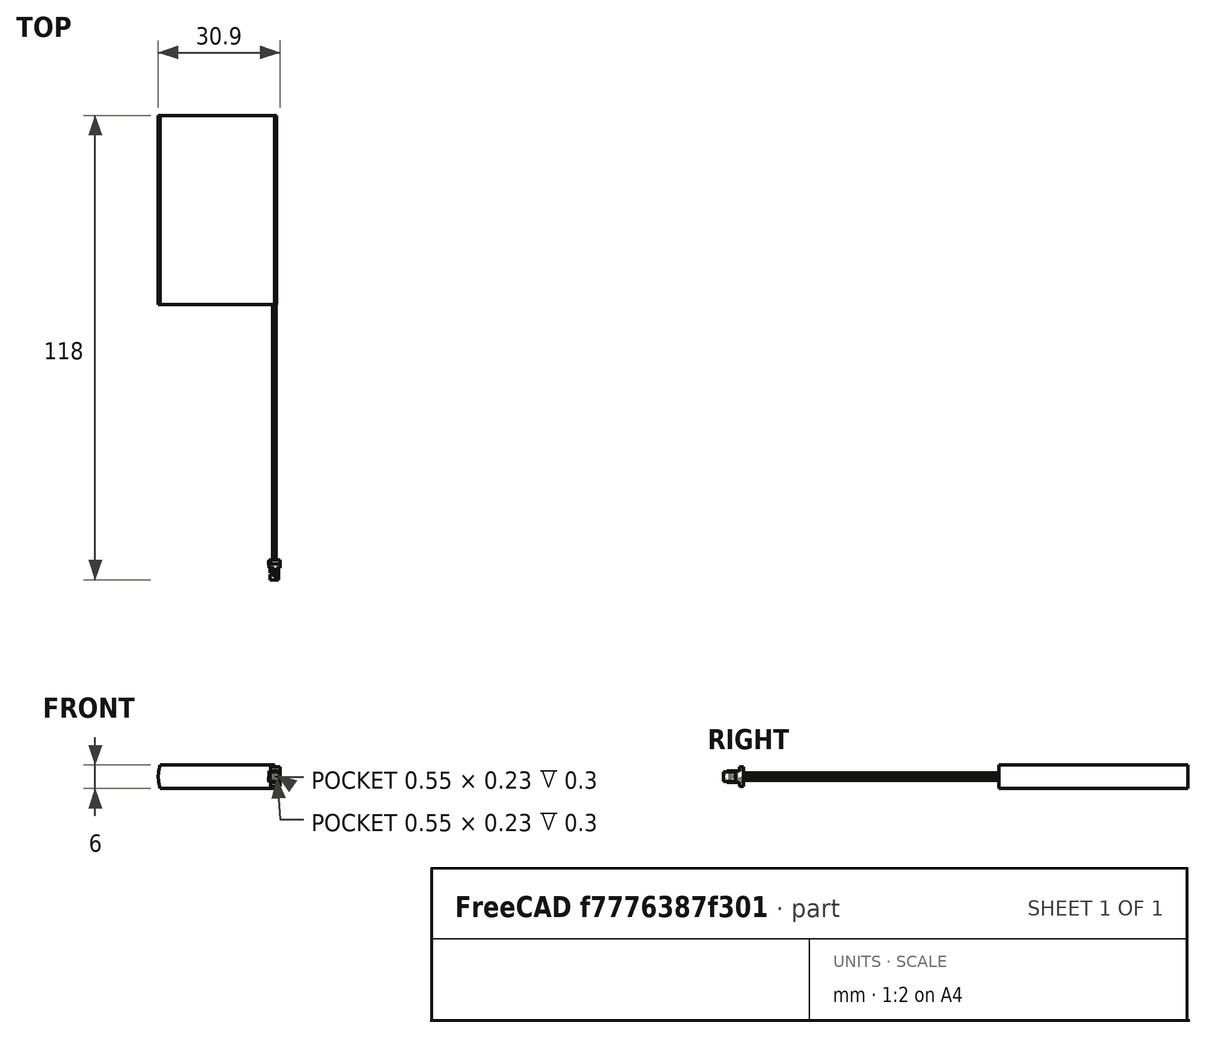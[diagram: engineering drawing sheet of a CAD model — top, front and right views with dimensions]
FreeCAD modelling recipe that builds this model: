
FCSTD DOCUMENT  (FreeCAD 2021.519R24301 +3652 (Git))
Label: ASR00036_850mAh
License: Other
objects: TechDraw::DrawViewDimension×4, Sketcher::SketchObject×3, PartDesign::Pad×3, TechDraw::DrawViewPart×2, TechDraw::DrawViewAnnotation×2, PartDesign::Pocket×1, PartDesign::Mirrored×1, PartDesign::Body×1, Part::Feature×1, Part::MultiFuse×1, TechDraw::DrawSVGTemplate×1, TechDraw::DrawPage×1, Mesh::Feature×1
note: 21 computed .brp shape members not serialized (recipe doc carries the construction recipe); baked Part::Feature solids carry a one-line shape summary decoded from their .brp

FEATURE [Sketcher::SketchObject] Sketch
  FullyConstrained = true
  MapMode = 5
  Support = -> [XY_Plane]
  sketch-geometry (4):
    g0: LineSegment StartX=-15 StartY=24 StartZ=0 EndX=15 EndY=24 EndZ=0
    g1: LineSegment StartX=15 StartY=24 StartZ=0 EndX=15 EndY=-24 EndZ=0
    g2: LineSegment StartX=15 StartY=-24 StartZ=0 EndX=-15 EndY=-24 EndZ=0
    g3: LineSegment StartX=-15 StartY=-24 StartZ=0 EndX=-15 EndY=24 EndZ=0
  constraints (10):
    c: Coincident(g0,g1)
    c: Coincident(g1,g2)
    c: Coincident(g2,g3)
    c: Coincident(g3,g0)
    c: Horizontal(g2)
    c: Vertical(g1)
    c: Symmetric(g0,g2,g-1)
    c: Symmetric(g0,g0,g-2)
    c: DistanceX(g0,g0) = 30
    c: DistanceY(g3,g3) = 48
FEATURE [PartDesign::Pad] Pad
  ClaimChildren = false
  Direction = (1,1,1)
  Fit = 0
  FitJoin = 0
  InnerFit = 0
  InnerFitJoin = 0
  InnerTaperAngle = 0
  InnerTaperAngleRev = 0
  Length = 6
  Length2 = 100
  Midplane = true
  NewSolid = false
  Profile = -> Sketch
  Suppress = false
  Type = 0
FEATURE [Sketcher::SketchObject] Sketch001
  ExternalGeometry = -> [Pad]
  FullyConstrained = true
  MapMode = 5
  Placement = pos=(0,24,0) rot=(0,0.707107,0.707107;3.14159rad)
  Support = -> [Pad]
  sketch-geometry (5):
    g0: ArcOfCircle CenterX=-5.75 CenterY=-6e-16 CenterZ=0 NormalX=0 NormalY=0 NormalZ=1 AngleXU=0 Radius=9.25 StartAngle=2.8113 EndAngle=3.47189
    g1: LineSegment [constr] StartX=-14.5 StartY=-3 StartZ=0 EndX=-14.5 EndY=3 EndZ=0
    g2: LineSegment StartX=-14.5 StartY=-3 StartZ=0 EndX=-16 EndY=-3 EndZ=0
    g3: LineSegment StartX=-14.5 StartY=3 StartZ=0 EndX=-16 EndY=3 EndZ=0
    g4: LineSegment StartX=-16 StartY=3 StartZ=0 EndX=-16 EndY=-3 EndZ=0
  constraints (15):
    c: PointOnObject(g0,g-5)
    c: PointOnObject(g0,g-4)
    c: Tangent(g0,g-3)
    c: Coincident(g1,g0)
    c: Coincident(g1,g0)
    c: Vertical(g1)
    c: Coincident(g2,g0)
    c: Horizontal(g2)
    c: Coincident(g3,g0)
    c: Horizontal(g3)
    c: Coincident(g4,g3)
    c: Coincident(g4,g2)
    c: Vertical(g4)
    c: DistanceX(g3,g-4) = 1
    c: DistanceX(g-4,g0) = 0.5
FEATURE [PartDesign::Pocket] Pocket
  BaseFeature = -> Pad
  ClaimChildren = false
  Fit = 0
  FitJoin = 0
  InnerFit = 0
  InnerFitJoin = 0
  InnerTaperAngle = 0
  InnerTaperAngleRev = 0
  Length = 5
  Length2 = 100
  NewSolid = false
  Profile = -> Sketch001
  Suppress = false
  Type = 1
FEATURE [PartDesign::Mirrored] Mirrored
  BaseFeature = -> Pocket
  CopyShape = true
  MirrorPlane = -> Sketch001 [V_Axis]
  NewSolid = false
  OriginalSubs = -> [Pocket]
  Originals = -> [Pocket]
  ParallelTransform = true
  SubTransform = true
  Suppress = false
FEATURE [PartDesign::Pad] Pad001
  BaseFeature = -> Mirrored
  ClaimChildren = false
  Direction = (1,1,1)
  Fit = 0
  FitJoin = 0
  InnerFit = 0
  InnerFitJoin = 0
  InnerTaperAngle = 0
  InnerTaperAngleRev = 0
  Length = 7.85
  Length2 = 100
  NewSolid = false
  Profile = -> Mirrored [Face8]
  Reversed = true
  Suppress = false
  Type = 0
FEATURE [Sketcher::SketchObject] Sketch002
  ExternalGeometry = -> [Pad001]
  FullyConstrained = true
  MapMode = 5
  Placement = pos=(0,-24,0) rot=(1,0,0;1.5708rad)
  Support = -> [Pad001]
  sketch-geometry (7):
    g0: Circle CenterX=14.5 CenterY=-0.5 CenterZ=0 NormalX=0 NormalY=0 NormalZ=1 AngleXU=0 Radius=0.45
    g1: Circle CenterX=14.5 CenterY=0.5 CenterZ=0 NormalX=0 NormalY=0 NormalZ=1 AngleXU=0 Radius=0.45
    g2: LineSegment [constr] StartX=14.5 StartY=0.5 StartZ=0 EndX=14.5 EndY=-0.5 EndZ=0
    g3: GeomPoint [constr] X=14.5 Y=-0.95 Z=0
    g4: GeomPoint [constr] X=14.5 Y=0.95 Z=0
    g5: LineSegment [constr] StartX=14.05 StartY=-0.5 StartZ=0 EndX=14.95 EndY=-0.5 EndZ=0
    g6: GeomPoint [constr] X=14.5 Y=0.05 Z=0
  constraints (16):
    c: Coincident(g2,g1)
    c: Coincident(g2,g0)
    c: Equal(g0,g1)
    c: Diameter(g0) = 0.9
    c: Symmetric(g0,g1,g-1)
    c: PointOnObject(g3,g2)
    c: PointOnObject(g4,g1)
    c: Symmetric(g3,g4,g-1)
    c: PointOnObject(g5,g0)
    c: PointOnObject(g5,g0)
    c: Horizontal(g5)
    c: PointOnObject(g0,g5)
    c: PointOnObject(g6,g1)
    c: PointOnObject(g6,g2)
    c: DistanceX(g5,g-3) = 0.05
    c: DistanceY(g-3,g6) = 0.05
FEATURE [PartDesign::Pad] Pad002
  BaseFeature = -> Pad001
  ClaimChildren = false
  Direction = (1,1,1)
  Fit = 0
  FitJoin = 0
  InnerFit = 0
  InnerFitJoin = 0
  InnerTaperAngle = 0
  InnerTaperAngleRev = 0
  Length = 65
  Length2 = 100
  NewSolid = false
  Profile = -> Sketch002
  Suppress = false
  Type = 0
FEATURE [PartDesign::Body] Body
  AutoGroupSolids = false
  ExportMode = 0
  Group = -> [Sketch,Pad,Sketch001,Pocket,Mirrored,Pad001,Sketch002,Pad002]
  Origin = -> Origin
  Tip = -> Pad002
  _ExportChildren = -> [Pad,Pocket,Mirrored,Pad001,Pad002]
  _GroupVersion = 1
FEATURE [Part::Feature] Solid  label="Body007"
  Placement = pos=(13.2155,-91,7.7e-15) rot=(0,0,1;0rad)
  shape: bbox 2.9 x 5 x 4.94 mm, 60 faces (baked)
FEATURE [Part::MultiFuse] Fusion
  Shapes = -> [Body,Solid]
FEATURE [TechDraw::DrawSVGTemplate] Template
  Height = 210
  Orientation = 1
  Width = 297
FEATURE [TechDraw::DrawViewPart] View
  CoarseView = false
  Direction = (0,0,1)
  Focus = 100
  HardHidden = false
  IsoCount = 0
  IsoHidden = false
  IsoVisible = false
  LockPosition = false
  Perspective = false
  Rotation = 180
  Scale = 0.927
  ScaleType = 0
  SeamHidden = false
  SeamVisible = true
  SmoothHidden = false
  SmoothVisible = true
  Source = -> [Fusion]
  X = 178.5
  XDirection = (1,0,0)
  Y = 105
FEATURE [TechDraw::DrawViewPart] View001
  CoarseView = false
  Direction = (-1,0,0)
  Focus = 100
  HardHidden = false
  IsoCount = 0
  IsoHidden = false
  IsoVisible = false
  LockPosition = false
  Perspective = false
  Rotation = 90
  Scale = 0.927
  ScaleType = 0
  SeamHidden = false
  SeamVisible = true
  SmoothHidden = false
  SmoothVisible = true
  Source = -> [Fusion]
  X = 118.5
  XDirection = (0,-1,0)
  Y = 105
FEATURE [TechDraw::DrawViewDimension] Dimension
  Arbitrary = false
  ArbitraryTolerances = false
  EqualTolerance = true
  FormatSpec = %.1f
  FormatSpecOverTolerance = %+.1f
  FormatSpecUnderTolerance = %+.1f
  Inverted = false
  LockPosition = false
  MeasureType = 1
  OverTolerance = 0.5
  References2D = -> [View001]
  Rotation = 0
  ScaleType = 0
  TheoreticalExact = false
  Type = 1
  UnderTolerance = -0.5
  X = -31
  Y = -59
FEATURE [TechDraw::DrawViewDimension] Dimension001
  Arbitrary = false
  ArbitraryTolerances = false
  EqualTolerance = true
  FormatSpec = %.1f
  FormatSpecOverTolerance = %+.1f
  FormatSpecUnderTolerance = %+.1f
  Inverted = false
  LockPosition = false
  MeasureType = 1
  OverTolerance = 2
  References2D = -> [View]
  Rotation = 0
  ScaleType = 0
  TheoreticalExact = false
  Type = 1
  UnderTolerance = -2
  X = 32.4171
  Y = -59
FEATURE [TechDraw::DrawViewDimension] Dimension002
  Arbitrary = false
  ArbitraryTolerances = false
  EqualTolerance = true
  FormatSpec = %.1f
  FormatSpecOverTolerance = %+.1f
  FormatSpecUnderTolerance = %+.1f
  Inverted = false
  LockPosition = false
  MeasureType = 1
  OverTolerance = 3
  References2D = -> [View]
  Rotation = 0
  ScaleType = 0
  TheoreticalExact = false
  Type = 2
  UnderTolerance = -3
  X = -30
  Y = -32.445
FEATURE [TechDraw::DrawViewDimension] Dimension003
  Arbitrary = false
  ArbitraryTolerances = false
  EqualTolerance = true
  FormatSpec = %.1f
  FormatSpecOverTolerance = %+.1f
  FormatSpecUnderTolerance = %+.1f
  Inverted = false
  LockPosition = false
  MeasureType = 1
  OverTolerance = 5
  References2D = -> [View]
  Rotation = 0
  ScaleType = 0
  TheoreticalExact = false
  Type = 2
  UnderTolerance = -5
  X = -30
  Y = 19.9305
FEATURE [TechDraw::DrawViewAnnotation] Annotation
  Font = MS Shell Dlg 2
  LineSpace = 80
  LockPosition = false
  MaxWidth = -1
  Rotation = 0
  ScaleType = 0
  Text = SIDE VIEW
  TextSize = 6
  TextStyle = 0
  X = 118.5
  Y = 162
FEATURE [TechDraw::DrawViewAnnotation] Annotation001
  Font = MS Shell Dlg 2
  LineSpace = 80
  LockPosition = false
  MaxWidth = -1
  Rotation = 0
  ScaleType = 0
  Text = TOP VIEW
  TextSize = 6
  TextStyle = 0
  X = 178.5
  Y = 162
FEATURE [TechDraw::DrawPage] Page
  KeepUpdated = true
  NextBalloonIndex = 1
  ProjectionType = 0
  Template = -> Template
  Views = -> [View,View001,Dimension,Dimension001,Dimension002,Dimension003,Annotation,Annotation001]
FEATURE [Mesh::Feature] Mesh  label="Fusion (Meshed)"
